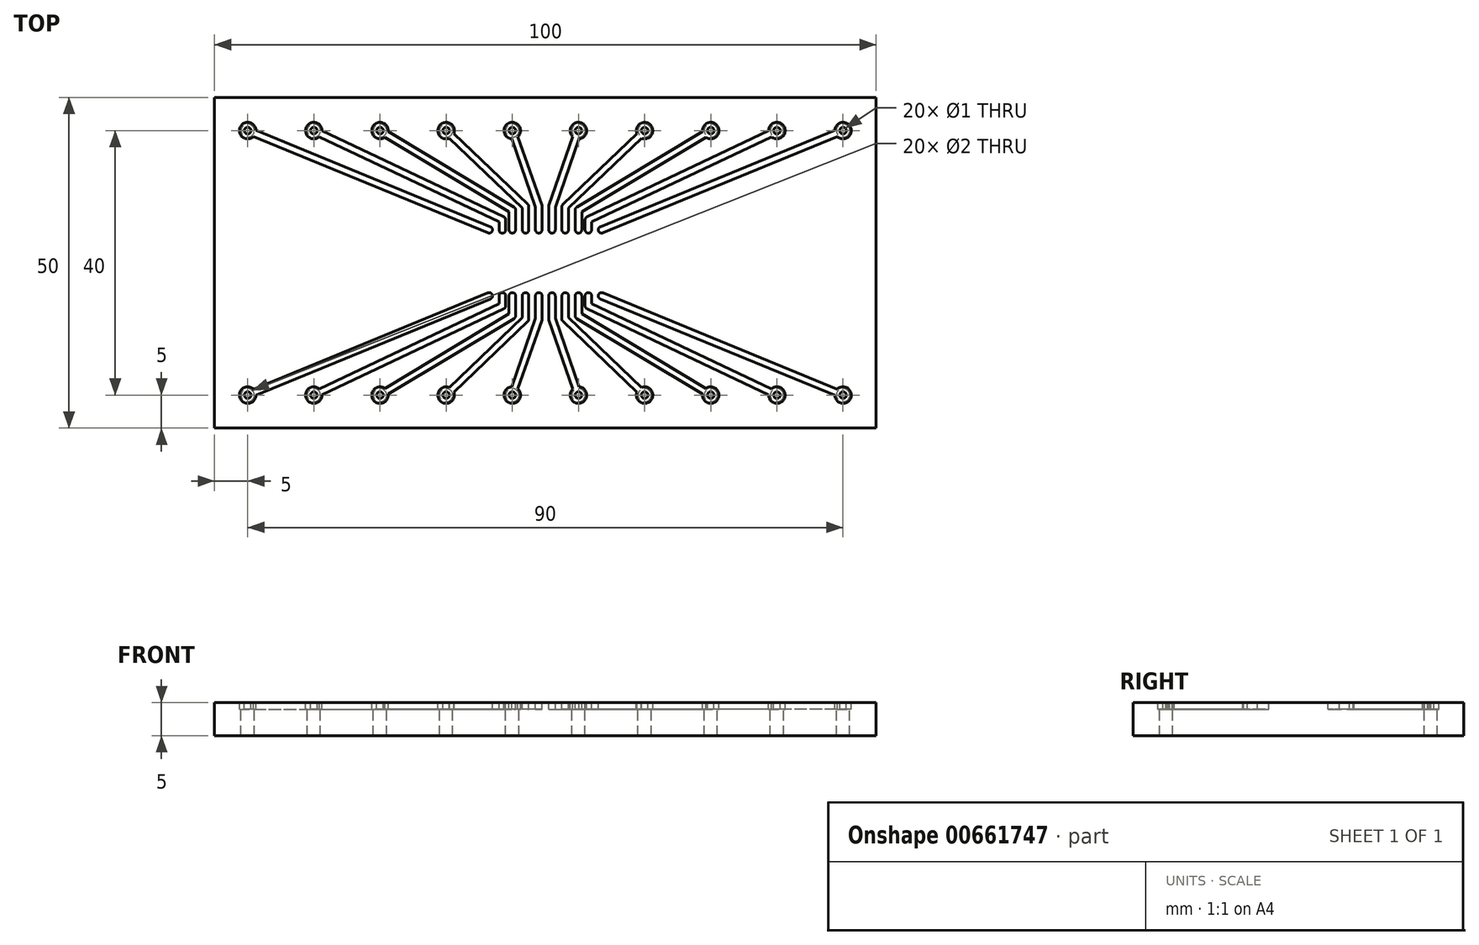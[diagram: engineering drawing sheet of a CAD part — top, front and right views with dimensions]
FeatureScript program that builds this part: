
annotation { "Feature Type Name" : "Feature", "Feature Type Description" : "" }
export const myFeature = defineFeature(function(context is Context, id is Id, definition is map)
    precondition{}
    {
        {
            var Q0;
            Q0=qCreatedBy(makeId("Top.planeOp"),FACE);
            var sketch = newSketch(context, id + "F0", { "sketchPlane" : qUnion([Q0])});
            skLineSegment(sketch, "E0.bottom", {"start": v(50, -25) * mm, "end": v(-50, -25) * mm});
            skLineSegment(sketch, "E0.top", {"start": v(50, 25) * mm, "end": v(-50, 25) * mm});
            skLineSegment(sketch, "E0.left", {"start": v(50, -25) * mm, "end": v(50, 25) * mm});
            skLineSegment(sketch, "E0.right", {"start": v(-50, -25) * mm, "end": v(-50, 25) * mm});
            skPoint(sketch, "E0.middle", {"position": v(0, 0) * mm});
            skSolve(sketch);
        }
        {
            var Q0;
            Q0=makeQuery(id+"F0.imprint","IMPRINT",FACE,{"disambiguationData":[TD([[makeQuery(id+"F0.imprint","IMPRINT",EDGE,{"derivedFrom":sQuery(id+"F0.wireOp",EDGE,"E0.bottom")}),-1.0]])]});
            extrude(context, id + "F1", {"entities" : qUnion([Q0]), "depth" : 5 * mm, "offsetDistance" : 25 * mm});
        }
        {
            var Q0;
            Q0=makeQuery(id+"F1.opExtrude","CAP_FACE",FACE,{"disambiguationData":[OSD([sQuery(id+"F0.wireOp",EDGE,"E0.bottom"),sQuery(id+"F0.wireOp",EDGE,"E0.top"),sQuery(id+"F0.wireOp",EDGE,"E0.left"),sQuery(id+"F0.wireOp",EDGE,"E0.right")])],"isStart":false});
            var sketch = newSketch(context, id + "F2", { "sketchPlane" : qUnion([Q0])});
            skPoint(sketch, "E1", {"position": v(-45, 20) * mm});
            skPoint(sketch, "E2.0.1.0", {"position": v(-45, -20) * mm});
            skPoint(sketch, "E2.1.0.0", {"position": v(-35, 20) * mm});
            skPoint(sketch, "E2.1.1.0", {"position": v(-35, -20) * mm});
            skPoint(sketch, "E2.2.0.0", {"position": v(-25, 20) * mm});
            skPoint(sketch, "E2.2.1.0", {"position": v(-25, -20) * mm});
            skPoint(sketch, "E2.3.0.0", {"position": v(-15, 20) * mm});
            skPoint(sketch, "E2.3.1.0", {"position": v(-15, -20) * mm});
            skPoint(sketch, "E2.4.0.0", {"position": v(-5, 20) * mm});
            skPoint(sketch, "E2.4.1.0", {"position": v(-5, -20) * mm});
            skPoint(sketch, "E2.5.0.0", {"position": v(5, 20) * mm});
            skPoint(sketch, "E2.5.1.0", {"position": v(5, -20) * mm});
            skPoint(sketch, "E2.6.0.0", {"position": v(15, 20) * mm});
            skPoint(sketch, "E2.6.1.0", {"position": v(15, -20) * mm});
            skPoint(sketch, "E2.7.0.0", {"position": v(25, 20) * mm});
            skPoint(sketch, "E2.7.1.0", {"position": v(25, -20) * mm});
            skPoint(sketch, "E2.8.0.0", {"position": v(35, 20) * mm});
            skPoint(sketch, "E2.8.1.0", {"position": v(35, -20) * mm});
            skPoint(sketch, "E2.9.0.0", {"position": v(45, 20) * mm});
            skPoint(sketch, "E2.9.1.0", {"position": v(45, -20) * mm});
            skLineSegment(sketch, "E2.direction1", {"start": v(-45, 20) * mm, "end": v(-35, 20) * mm, "construction": true});
            skLineSegment(sketch, "E2.direction2", {"start": v(-45, 20) * mm, "end": v(-45, -20) * mm, "construction": true});
            skLineSegment(sketch, "E3.bottom", {"start": v(10.5, 5) * mm, "end": v(-9.5, 5) * mm});
            skLineSegment(sketch, "E3.top", {"start": v(9.5, -5) * mm, "end": v(-10.5, -5) * mm});
            skPoint(sketch, "E3.middle", {"position": v(0, 0) * mm});
            skPoint(sketch, "E4", {"position": v(-8.5, 5) * mm});
            skPoint(sketch, "E5.0.1.0", {"position": v(-9, -5) * mm});
            skPoint(sketch, "E5.1.0.0", {"position": v(-6.5, 5) * mm});
            skPoint(sketch, "E5.1.1.0", {"position": v(-7, -5) * mm});
            skPoint(sketch, "E5.2.0.0", {"position": v(-5, 5) * mm});
            skPoint(sketch, "E5.2.1.0", {"position": v(-5, -5) * mm});
            skPoint(sketch, "E5.3.0.0", {"position": v(-3, 5) * mm});
            skPoint(sketch, "E5.3.1.0", {"position": v(-3, -5) * mm});
            skPoint(sketch, "E5.4.0.0", {"position": v(-1, 5) * mm});
            skPoint(sketch, "E5.4.1.0", {"position": v(-1, -5) * mm});
            skPoint(sketch, "E5.5.0.0", {"position": v(1, 5) * mm});
            skPoint(sketch, "E5.5.1.0", {"position": v(1, -5) * mm});
            skPoint(sketch, "E5.6.0.0", {"position": v(3, 5) * mm});
            skPoint(sketch, "E5.6.1.0", {"position": v(3, -5) * mm});
            skPoint(sketch, "E5.7.0.0", {"position": v(5, 5) * mm});
            skPoint(sketch, "E5.7.1.0", {"position": v(5, -5) * mm});
            skPoint(sketch, "E5.8.0.0", {"position": v(7, 5) * mm});
            skPoint(sketch, "E5.8.1.0", {"position": v(7, -5) * mm});
            skPoint(sketch, "E5.9.0.0", {"position": v(9, 5) * mm});
            skPoint(sketch, "E5.9.1.0", {"position": v(9, -5) * mm});
            skLineSegment(sketch, "E5.direction1", {"start": v(-8.5, 5) * mm, "end": v(-6.5, 5) * mm, "construction": true});
            skLineSegment(sketch, "E6", {"start": v(-45, 20) * mm, "end": v(-8.5, 5) * mm});
            skArc(sketch, "E7.0.startCap", {"start": v(-45.2, 19.54) * mm, "mid": v(-45.46, 20.2) * mm, "end": v(-44.8, 20.46) * mm});
            skArc(sketch, "E7.0.endCap", {"start": v(-8.3, 5.46) * mm, "mid": v(-8.04, 4.8) * mm, "end": v(-8.69, 4.54) * mm});
            skLineSegment(sketch, "E7.0.left", {"start": v(-44.8, 20.46) * mm, "end": v(-8.3, 5.46) * mm});
            skLineSegment(sketch, "E7.0.right", {"start": v(-45.2, 19.54) * mm, "end": v(-8.69, 4.54) * mm});
            skLineSegment(sketch, "E8", {"start": v(-6.5, 5) * mm, "end": v(-6.5, 6.5) * mm});
            skLineSegment(sketch, "E9", {"start": v(-35, 20) * mm, "end": v(-6.5, 6.5) * mm});
            skArc(sketch, "E10.0.startCap", {"start": v(-6, 5) * mm, "mid": v(-6.5, 4.5) * mm, "end": v(-7, 5) * mm});
            skArc(sketch, "E10.0.endCap", {"start": v(-7, 6.5) * mm, "mid": v(-6.5, 7) * mm, "end": v(-6, 6.5) * mm});
            skLineSegment(sketch, "E10.0.left", {"start": v(-7, 5) * mm, "end": v(-7, 6.5) * mm});
            skLineSegment(sketch, "E10.0.right", {"start": v(-6, 5) * mm, "end": v(-6, 6.5) * mm});
            skArc(sketch, "E10.1.startCap", {"start": v(-35.21, 19.55) * mm, "mid": v(-35.45, 20.21) * mm, "end": v(-34.79, 20.45) * mm});
            skArc(sketch, "E10.1.endCap", {"start": v(-6.29, 6.95) * mm, "mid": v(-6.05, 6.29) * mm, "end": v(-6.71, 6.05) * mm});
            skLineSegment(sketch, "E10.1.left", {"start": v(-34.79, 20.45) * mm, "end": v(-6.29, 6.95) * mm});
            skLineSegment(sketch, "E10.1.right", {"start": v(-35.21, 19.55) * mm, "end": v(-6.71, 6.05) * mm});
            skLineSegment(sketch, "E11", {"start": v(-5, 5) * mm, "end": v(-5, 8) * mm});
            skLineSegment(sketch, "E12", {"start": v(-5, 8) * mm, "end": v(-25, 20) * mm});
            skLineSegment(sketch, "E13", {"start": v(-3, 5) * mm, "end": v(-3, 8.5) * mm});
            skLineSegment(sketch, "E14", {"start": v(-3, 8.5) * mm, "end": v(-15, 20) * mm});
            skLineSegment(sketch, "E15", {"start": v(-1, 5) * mm, "end": v(-1, 8.5) * mm});
            skLineSegment(sketch, "E16", {"start": v(-1, 8.5) * mm, "end": v(-5, 20) * mm});
            skArc(sketch, "E17.0.startCap", {"start": v(-4.5, 5) * mm, "mid": v(-5, 4.5) * mm, "end": v(-5.5, 5) * mm});
            skArc(sketch, "E17.0.endCap", {"start": v(-5.5, 8) * mm, "mid": v(-5, 8.5) * mm, "end": v(-4.5, 8) * mm});
            skLineSegment(sketch, "E17.0.left", {"start": v(-5.5, 5) * mm, "end": v(-5.5, 8) * mm});
            skLineSegment(sketch, "E17.0.right", {"start": v(-4.5, 5) * mm, "end": v(-4.5, 8) * mm});
            skArc(sketch, "E17.1.startCap", {"start": v(-2.65, 8.86) * mm, "mid": v(-2.64, 8.15) * mm, "end": v(-3.35, 8.14) * mm});
            skArc(sketch, "E17.1.endCap", {"start": v(-15.35, 19.64) * mm, "mid": v(-15.36, 20.35) * mm, "end": v(-14.65, 20.36) * mm});
            skLineSegment(sketch, "E17.1.left", {"start": v(-3.35, 8.14) * mm, "end": v(-15.35, 19.64) * mm});
            skLineSegment(sketch, "E17.1.right", {"start": v(-2.65, 8.86) * mm, "end": v(-14.65, 20.36) * mm});
            skArc(sketch, "E17.2.startCap", {"start": v(-0.53, 8.66) * mm, "mid": v(-0.84, 8.03) * mm, "end": v(-1.47, 8.34) * mm});
            skArc(sketch, "E17.2.endCap", {"start": v(-5.47, 19.84) * mm, "mid": v(-5.16, 20.47) * mm, "end": v(-4.53, 20.16) * mm});
            skLineSegment(sketch, "E17.2.left", {"start": v(-1.47, 8.34) * mm, "end": v(-5.47, 19.84) * mm});
            skLineSegment(sketch, "E17.2.right", {"start": v(-0.53, 8.66) * mm, "end": v(-4.53, 20.16) * mm});
            skArc(sketch, "E17.3.startCap", {"start": v(-2.5, 5) * mm, "mid": v(-3, 4.5) * mm, "end": v(-3.5, 5) * mm});
            skArc(sketch, "E17.3.endCap", {"start": v(-3.5, 8.5) * mm, "mid": v(-3, 9) * mm, "end": v(-2.5, 8.5) * mm});
            skLineSegment(sketch, "E17.3.left", {"start": v(-3.5, 5) * mm, "end": v(-3.5, 8.5) * mm});
            skLineSegment(sketch, "E17.3.right", {"start": v(-2.5, 5) * mm, "end": v(-2.5, 8.5) * mm});
            skArc(sketch, "E17.4.startCap", {"start": v(-0.5, 5) * mm, "mid": v(-1, 4.5) * mm, "end": v(-1.5, 5) * mm});
            skArc(sketch, "E17.4.endCap", {"start": v(-1.5, 8.5) * mm, "mid": v(-1, 9) * mm, "end": v(-0.5, 8.5) * mm});
            skLineSegment(sketch, "E17.4.left", {"start": v(-1.5, 5) * mm, "end": v(-1.5, 8.5) * mm});
            skLineSegment(sketch, "E17.4.right", {"start": v(-0.5, 5) * mm, "end": v(-0.5, 8.5) * mm});
            skArc(sketch, "E17.5.startCap", {"start": v(-4.74, 8.43) * mm, "mid": v(-4.57, 7.74) * mm, "end": v(-5.26, 7.57) * mm});
            skArc(sketch, "E17.5.endCap", {"start": v(-25.26, 19.57) * mm, "mid": v(-25.43, 20.26) * mm, "end": v(-24.74, 20.43) * mm});
            skLineSegment(sketch, "E17.5.left", {"start": v(-5.26, 7.57) * mm, "end": v(-25.26, 19.57) * mm});
            skLineSegment(sketch, "E17.5.right", {"start": v(-4.74, 8.43) * mm, "end": v(-24.74, 20.43) * mm});
            skLineSegment(sketch, "E18.MirrorCS", {"start": v(44.8, 20.46) * mm, "end": v(8.3, 5.46) * mm});
            skLineSegment(sketch, "E19.MirrorCS", {"start": v(35, 20) * mm, "end": v(6.5, 6.5) * mm});
            skArc(sketch, "E20.MirrorCS", {"start": v(7, 6.5) * mm, "mid": v(6.5, 7) * mm, "end": v(6, 6.5) * mm});
            skLineSegment(sketch, "E21.MirrorCS", {"start": v(3.5, 5) * mm, "end": v(3.5, 8.5) * mm});
            skArc(sketch, "E22.MirrorCS", {"start": v(5.5, 8) * mm, "mid": v(5, 8.5) * mm, "end": v(4.5, 8) * mm});
            skLineSegment(sketch, "E23.MirrorCS", {"start": v(4.74, 8.43) * mm, "end": v(24.74, 20.43) * mm});
            skArc(sketch, "E24.MirrorCS", {"start": v(5.47, 19.84) * mm, "mid": v(5.16, 20.47) * mm, "end": v(4.53, 20.16) * mm});
            skArc(sketch, "E25.MirrorCS", {"start": v(0.5, 5) * mm, "mid": v(1, 4.5) * mm, "end": v(1.5, 5) * mm});
            skLineSegment(sketch, "E26.MirrorCS", {"start": v(7, 5) * mm, "end": v(7, 6.5) * mm});
            skLineSegment(sketch, "E27.MirrorCS", {"start": v(2.5, 5) * mm, "end": v(2.5, 8.5) * mm});
            skLineSegment(sketch, "E28.MirrorCS", {"start": v(5.5, 5) * mm, "end": v(5.5, 8) * mm});
            skLineSegment(sketch, "E29.MirrorCS", {"start": v(5, 5) * mm, "end": v(5, 8) * mm});
            skLineSegment(sketch, "E30.MirrorCS", {"start": v(4.5, 5) * mm, "end": v(4.5, 8) * mm});
            skLineSegment(sketch, "E31.MirrorCS", {"start": v(6, 5) * mm, "end": v(6, 6.5) * mm});
            skArc(sketch, "E32.MirrorCS", {"start": v(1.5, 8.5) * mm, "mid": v(1, 9) * mm, "end": v(0.5, 8.5) * mm});
            skLineSegment(sketch, "E33.MirrorCS", {"start": v(5, 8) * mm, "end": v(25, 20) * mm});
            skArc(sketch, "E34.MirrorCS", {"start": v(2.65, 8.86) * mm, "mid": v(2.64, 8.15) * mm, "end": v(3.35, 8.14) * mm});
            skArc(sketch, "E35.MirrorCS", {"start": v(35.21, 19.55) * mm, "mid": v(35.45, 20.21) * mm, "end": v(34.79, 20.45) * mm});
            skLineSegment(sketch, "E36.MirrorCS", {"start": v(1.47, 8.34) * mm, "end": v(5.47, 19.84) * mm});
            skLineSegment(sketch, "E37.MirrorCS", {"start": v(45, 20) * mm, "end": v(8.5, 5) * mm});
            skArc(sketch, "E38.MirrorCS", {"start": v(8.3, 5.46) * mm, "mid": v(8.04, 4.8) * mm, "end": v(8.69, 4.54) * mm});
            skLineSegment(sketch, "E39.MirrorCS", {"start": v(6.5, 5) * mm, "end": v(6.5, 6.5) * mm});
            skLineSegment(sketch, "E40.MirrorCS", {"start": v(3, 5) * mm, "end": v(3, 8.5) * mm});
            skLineSegment(sketch, "E41.MirrorCS", {"start": v(45.2, 19.54) * mm, "end": v(8.69, 4.54) * mm});
            skArc(sketch, "E42.MirrorCS", {"start": v(6, 5) * mm, "mid": v(6.5, 4.5) * mm, "end": v(7, 5) * mm});
            skArc(sketch, "E43.MirrorCS", {"start": v(15.35, 19.64) * mm, "mid": v(15.36, 20.35) * mm, "end": v(14.65, 20.36) * mm});
            skLineSegment(sketch, "E44.MirrorCS", {"start": v(1.5, 5) * mm, "end": v(1.5, 8.5) * mm});
            skArc(sketch, "E45.MirrorCS", {"start": v(6.29, 6.95) * mm, "mid": v(6.05, 6.29) * mm, "end": v(6.71, 6.05) * mm});
            skLineSegment(sketch, "E46.MirrorCS", {"start": v(0.53, 8.66) * mm, "end": v(4.53, 20.16) * mm});
            skLineSegment(sketch, "E47.MirrorCS", {"start": v(0.5, 5) * mm, "end": v(0.5, 8.5) * mm});
            skArc(sketch, "E48.MirrorCS", {"start": v(4.74, 8.43) * mm, "mid": v(4.57, 7.74) * mm, "end": v(5.26, 7.57) * mm});
            skLineSegment(sketch, "E49.MirrorCS", {"start": v(3, 8.5) * mm, "end": v(15, 20) * mm});
            skLineSegment(sketch, "E50.MirrorCS", {"start": v(3.35, 8.14) * mm, "end": v(15.35, 19.64) * mm});
            skLineSegment(sketch, "E51.MirrorCS", {"start": v(34.79, 20.45) * mm, "end": v(6.29, 6.95) * mm});
            skArc(sketch, "E52.MirrorCS", {"start": v(2.5, 5) * mm, "mid": v(3, 4.5) * mm, "end": v(3.5, 5) * mm});
            skArc(sketch, "E53.MirrorCS", {"start": v(25.26, 19.57) * mm, "mid": v(25.43, 20.26) * mm, "end": v(24.74, 20.43) * mm});
            skLineSegment(sketch, "E54.MirrorCS", {"start": v(1, 5) * mm, "end": v(1, 8.5) * mm});
            skLineSegment(sketch, "E55.MirrorCS", {"start": v(2.65, 8.86) * mm, "end": v(14.65, 20.36) * mm});
            skLineSegment(sketch, "E56.MirrorCS", {"start": v(35.21, 19.55) * mm, "end": v(6.71, 6.05) * mm});
            skArc(sketch, "E57.MirrorCS", {"start": v(3.5, 8.5) * mm, "mid": v(3, 9) * mm, "end": v(2.5, 8.5) * mm});
            skArc(sketch, "E58.MirrorCS", {"start": v(4.5, 5) * mm, "mid": v(5, 4.5) * mm, "end": v(5.5, 5) * mm});
            skLineSegment(sketch, "E59.MirrorCS", {"start": v(5.26, 7.57) * mm, "end": v(25.26, 19.57) * mm});
            skLineSegment(sketch, "E60.MirrorCS", {"start": v(1, 8.5) * mm, "end": v(5, 20) * mm});
            skArc(sketch, "E61.MirrorCS", {"start": v(0.53, 8.66) * mm, "mid": v(0.84, 8.03) * mm, "end": v(1.47, 8.34) * mm});
            skArc(sketch, "E62.MirrorCS", {"start": v(45.2, 19.54) * mm, "mid": v(45.46, 20.2) * mm, "end": v(44.8, 20.46) * mm});
            skArc(sketch, "E63.MirrorCS", {"start": v(2.5, -5) * mm, "mid": v(3, -4.5) * mm, "end": v(3.5, -5) * mm});
            skArc(sketch, "E64.MirrorCS", {"start": v(-3.5, -8.5) * mm, "mid": v(-3, -9) * mm, "end": v(-2.5, -8.5) * mm});
            skLineSegment(sketch, "E65.MirrorCS", {"start": v(44.8, -20.46) * mm, "end": v(8.3, -5.46) * mm});
            skLineSegment(sketch, "E66.MirrorCS", {"start": v(4.74, -8.43) * mm, "end": v(24.74, -20.43) * mm});
            skArc(sketch, "E67.MirrorCS", {"start": v(2.65, -8.86) * mm, "mid": v(2.64, -8.15) * mm, "end": v(3.35, -8.14) * mm});
            skLineSegment(sketch, "E68.MirrorCS", {"start": v(6.5, -5) * mm, "end": v(6.5, -6.5) * mm});
            skLineSegment(sketch, "E69.MirrorCS", {"start": v(3.35, -8.14) * mm, "end": v(15.35, -19.64) * mm});
            skPoint(sketch, "E70.MirrorP", {"position": v(-6.5, -5) * mm});
            skLineSegment(sketch, "E71.MirrorCS", {"start": v(-8.5, -5) * mm, "end": v(-6.5, -5) * mm, "construction": true});
            skLineSegment(sketch, "E72.MirrorCS", {"start": v(2.65, -8.86) * mm, "end": v(14.65, -20.36) * mm});
            skLineSegment(sketch, "E73.MirrorCS", {"start": v(-5.5, -5) * mm, "end": v(-5.5, -8) * mm});
            skLineSegment(sketch, "E74.MirrorCS", {"start": v(-7, -5) * mm, "end": v(-7, -6.5) * mm});
            skLineSegment(sketch, "E75.MirrorCS", {"start": v(-1.5, -5) * mm, "end": v(-1.5, -8.5) * mm});
            skArc(sketch, "E76.MirrorCS", {"start": v(-2.65, -8.86) * mm, "mid": v(-2.64, -8.15) * mm, "end": v(-3.35, -8.14) * mm});
            skLineSegment(sketch, "E77.MirrorCS", {"start": v(5.5, -5) * mm, "end": v(5.5, -8) * mm});
            skArc(sketch, "E78.MirrorCS", {"start": v(-4.74, -8.43) * mm, "mid": v(-4.57, -7.74) * mm, "end": v(-5.26, -7.57) * mm});
            skLineSegment(sketch, "E79.MirrorCS", {"start": v(1.5, -5) * mm, "end": v(1.5, -8.5) * mm});
            skLineSegment(sketch, "E80.MirrorCS", {"start": v(4.5, -5) * mm, "end": v(4.5, -8) * mm});
            skArc(sketch, "E81.MirrorCS", {"start": v(-6.29, -6.95) * mm, "mid": v(-6.05, -6.29) * mm, "end": v(-6.71, -6.05) * mm});
            skLineSegment(sketch, "E82.MirrorCS", {"start": v(1, -8.5) * mm, "end": v(5, -20) * mm});
            skLineSegment(sketch, "E83.MirrorCS", {"start": v(0.53, -8.66) * mm, "end": v(4.53, -20.16) * mm});
            skLineSegment(sketch, "E84.MirrorCS", {"start": v(-3, -5) * mm, "end": v(-3, -8.5) * mm});
            skLineSegment(sketch, "E85.MirrorCS", {"start": v(-2.65, -8.86) * mm, "end": v(-14.65, -20.36) * mm});
            skLineSegment(sketch, "E86.MirrorCS", {"start": v(-45, -20) * mm, "end": v(-8.5, -5) * mm});
            skArc(sketch, "E87.MirrorCS", {"start": v(45.2, -19.54) * mm, "mid": v(45.46, -20.2) * mm, "end": v(44.8, -20.46) * mm});
            skArc(sketch, "E88.MirrorCS", {"start": v(-2.5, -5) * mm, "mid": v(-3, -4.5) * mm, "end": v(-3.5, -5) * mm});
            skLineSegment(sketch, "E89.MirrorCS", {"start": v(-4.74, -8.43) * mm, "end": v(-24.74, -20.43) * mm});
            skArc(sketch, "E90.MirrorCS", {"start": v(5.5, -8) * mm, "mid": v(5, -8.5) * mm, "end": v(4.5, -8) * mm});
            skLineSegment(sketch, "E91.MirrorCS", {"start": v(5, -8) * mm, "end": v(25, -20) * mm});
            skArc(sketch, "E92.MirrorCS", {"start": v(-45.2, -19.54) * mm, "mid": v(-45.46, -20.2) * mm, "end": v(-44.8, -20.46) * mm});
            skArc(sketch, "E93.MirrorCS", {"start": v(8.3, -5.46) * mm, "mid": v(8.04, -4.8) * mm, "end": v(8.69, -4.54) * mm});
            skLineSegment(sketch, "E94.MirrorCS", {"start": v(3, -8.5) * mm, "end": v(15, -20) * mm});
            skLineSegment(sketch, "E95.MirrorCS", {"start": v(-1, -8.5) * mm, "end": v(-5, -20) * mm});
            skLineSegment(sketch, "E96.MirrorCS", {"start": v(1, -5) * mm, "end": v(1, -8.5) * mm});
            skLineSegment(sketch, "E97.MirrorCS", {"start": v(-2.5, -5) * mm, "end": v(-2.5, -8.5) * mm});
            skArc(sketch, "E98.MirrorCS", {"start": v(-8.3, -5.46) * mm, "mid": v(-8.04, -4.8) * mm, "end": v(-8.69, -4.54) * mm});
            skArc(sketch, "E99.MirrorCS", {"start": v(0.5, -5) * mm, "mid": v(1, -4.5) * mm, "end": v(1.5, -5) * mm});
            skLineSegment(sketch, "E100.MirrorCS", {"start": v(45.2, -19.54) * mm, "end": v(8.69, -4.54) * mm});
            skLineSegment(sketch, "E101.MirrorCS", {"start": v(-44.8, -20.46) * mm, "end": v(-8.3, -5.46) * mm});
            skArc(sketch, "E102.MirrorCS", {"start": v(-5.5, -8) * mm, "mid": v(-5, -8.5) * mm, "end": v(-4.5, -8) * mm});
            skArc(sketch, "E103.MirrorCS", {"start": v(-7, -6.5) * mm, "mid": v(-6.5, -7) * mm, "end": v(-6, -6.5) * mm});
            skArc(sketch, "E104.MirrorCS", {"start": v(3.5, -8.5) * mm, "mid": v(3, -9) * mm, "end": v(2.5, -8.5) * mm});
            skArc(sketch, "E105.MirrorCS", {"start": v(-1.5, -8.5) * mm, "mid": v(-1, -9) * mm, "end": v(-0.5, -8.5) * mm});
            skLineSegment(sketch, "E106.MirrorCS", {"start": v(-6.5, -5) * mm, "end": v(-6.5, -6.5) * mm});
            skLineSegment(sketch, "E107.MirrorCS", {"start": v(-4.5, -5) * mm, "end": v(-4.5, -8) * mm});
            skLineSegment(sketch, "E108.MirrorCS", {"start": v(-45.2, -19.54) * mm, "end": v(-8.69, -4.54) * mm});
            skLineSegment(sketch, "E109.MirrorCS", {"start": v(2.5, -5) * mm, "end": v(2.5, -8.5) * mm});
            skLineSegment(sketch, "E110.MirrorCS", {"start": v(-0.5, -5) * mm, "end": v(-0.5, -8.5) * mm});
            skArc(sketch, "E111.MirrorCS", {"start": v(15.35, -19.64) * mm, "mid": v(15.36, -20.35) * mm, "end": v(14.65, -20.36) * mm});
            skLineSegment(sketch, "E112.MirrorCS", {"start": v(5, -5) * mm, "end": v(5, -8) * mm});
            skLineSegment(sketch, "E113.MirrorCS", {"start": v(-35, -20) * mm, "end": v(-6.5, -6.5) * mm});
            skArc(sketch, "E114.MirrorCS", {"start": v(-35.21, -19.55) * mm, "mid": v(-35.45, -20.21) * mm, "end": v(-34.79, -20.45) * mm});
            skLineSegment(sketch, "E115.MirrorCS", {"start": v(5.26, -7.57) * mm, "end": v(25.26, -19.57) * mm});
            skArc(sketch, "E116.MirrorCS", {"start": v(6.29, -6.95) * mm, "mid": v(6.05, -6.29) * mm, "end": v(6.71, -6.05) * mm});
            skLineSegment(sketch, "E117.MirrorCS", {"start": v(-5, -8) * mm, "end": v(-25, -20) * mm});
            skLineSegment(sketch, "E118.MirrorCS", {"start": v(-3.35, -8.14) * mm, "end": v(-15.35, -19.64) * mm});
            skArc(sketch, "E119.MirrorCS", {"start": v(0.53, -8.66) * mm, "mid": v(0.84, -8.03) * mm, "end": v(1.47, -8.34) * mm});
            skLineSegment(sketch, "E120.MirrorCS", {"start": v(-0.53, -8.66) * mm, "end": v(-4.53, -20.16) * mm});
            skArc(sketch, "E121.MirrorCS", {"start": v(-6, -5) * mm, "mid": v(-6.5, -4.5) * mm, "end": v(-7, -5) * mm});
            skLineSegment(sketch, "E122.MirrorCS", {"start": v(-5.26, -7.57) * mm, "end": v(-25.26, -19.57) * mm});
            skLineSegment(sketch, "E123.MirrorCS", {"start": v(3.5, -5) * mm, "end": v(3.5, -8.5) * mm});
            skArc(sketch, "E124.MirrorCS", {"start": v(1.5, -8.5) * mm, "mid": v(1, -9) * mm, "end": v(0.5, -8.5) * mm});
            skLineSegment(sketch, "E125.MirrorCS", {"start": v(-35.21, -19.55) * mm, "end": v(-6.71, -6.05) * mm});
            skLineSegment(sketch, "E126.MirrorCS", {"start": v(45, -20) * mm, "end": v(8.5, -5) * mm});
            skArc(sketch, "E127.MirrorCS", {"start": v(4.74, -8.43) * mm, "mid": v(4.57, -7.74) * mm, "end": v(5.26, -7.57) * mm});
            skLineSegment(sketch, "E128.MirrorCS", {"start": v(-1, -5) * mm, "end": v(-1, -8.5) * mm});
            skArc(sketch, "E129.MirrorCS", {"start": v(-5.47, -19.84) * mm, "mid": v(-5.16, -20.47) * mm, "end": v(-4.53, -20.16) * mm});
            skArc(sketch, "E130.MirrorCS", {"start": v(25.26, -19.57) * mm, "mid": v(25.43, -20.26) * mm, "end": v(24.74, -20.43) * mm});
            skLineSegment(sketch, "E131.MirrorCS", {"start": v(-3.5, -5) * mm, "end": v(-3.5, -8.5) * mm});
            skLineSegment(sketch, "E132.MirrorCS", {"start": v(35, -20) * mm, "end": v(6.5, -6.5) * mm});
            skArc(sketch, "E133.MirrorCS", {"start": v(5.47, -19.84) * mm, "mid": v(5.16, -20.47) * mm, "end": v(4.53, -20.16) * mm});
            skArc(sketch, "E134.MirrorCS", {"start": v(35.21, -19.55) * mm, "mid": v(35.45, -20.21) * mm, "end": v(34.79, -20.45) * mm});
            skLineSegment(sketch, "E135.MirrorCS", {"start": v(-45, -20) * mm, "end": v(-35, -20) * mm, "construction": true});
            skLineSegment(sketch, "E136.MirrorCS", {"start": v(3, -5) * mm, "end": v(3, -8.5) * mm});
            skLineSegment(sketch, "E137.MirrorCS", {"start": v(34.79, -20.45) * mm, "end": v(6.29, -6.95) * mm});
            skArc(sketch, "E138.MirrorCS", {"start": v(-4.5, -5) * mm, "mid": v(-5, -4.5) * mm, "end": v(-5.5, -5) * mm});
            skLineSegment(sketch, "E139.MirrorCS", {"start": v(35.21, -19.55) * mm, "end": v(6.71, -6.05) * mm});
            skArc(sketch, "E140.MirrorCS", {"start": v(-0.5, -5) * mm, "mid": v(-1, -4.5) * mm, "end": v(-1.5, -5) * mm});
            skLineSegment(sketch, "E141.MirrorCS", {"start": v(7, -5) * mm, "end": v(7, -6.5) * mm});
            skArc(sketch, "E142.MirrorCS", {"start": v(6, -5) * mm, "mid": v(6.5, -4.5) * mm, "end": v(7, -5) * mm});
            skLineSegment(sketch, "E143.MirrorCS", {"start": v(10.5, -5) * mm, "end": v(-9.5, -5) * mm});
            skLineSegment(sketch, "E144.MirrorCS", {"start": v(-6, -5) * mm, "end": v(-6, -6.5) * mm});
            skArc(sketch, "E145.MirrorCS", {"start": v(4.5, -5) * mm, "mid": v(5, -4.5) * mm, "end": v(5.5, -5) * mm});
            skLineSegment(sketch, "E146.MirrorCS", {"start": v(-5, -5) * mm, "end": v(-5, -8) * mm});
            skArc(sketch, "E147.MirrorCS", {"start": v(-15.35, -19.64) * mm, "mid": v(-15.36, -20.35) * mm, "end": v(-14.65, -20.36) * mm});
            skLineSegment(sketch, "E148.MirrorCS", {"start": v(-1.47, -8.34) * mm, "end": v(-5.47, -19.84) * mm});
            skArc(sketch, "E149.MirrorCS", {"start": v(-25.26, -19.57) * mm, "mid": v(-25.43, -20.26) * mm, "end": v(-24.74, -20.43) * mm});
            skArc(sketch, "E150.MirrorCS", {"start": v(7, -6.5) * mm, "mid": v(6.5, -7) * mm, "end": v(6, -6.5) * mm});
            skLineSegment(sketch, "E151.MirrorCS", {"start": v(6, -5) * mm, "end": v(6, -6.5) * mm});
            skLineSegment(sketch, "E152.MirrorCS", {"start": v(-34.79, -20.45) * mm, "end": v(-6.29, -6.95) * mm});
            skLineSegment(sketch, "E153.MirrorCS", {"start": v(1.47, -8.34) * mm, "end": v(5.47, -19.84) * mm});
            skLineSegment(sketch, "E154.MirrorCS", {"start": v(0.5, -5) * mm, "end": v(0.5, -8.5) * mm});
            skLineSegment(sketch, "E155.MirrorCS", {"start": v(-3, -8.5) * mm, "end": v(-15, -20) * mm});
            skArc(sketch, "E156.MirrorCS", {"start": v(-0.53, -8.66) * mm, "mid": v(-0.84, -8.03) * mm, "end": v(-1.47, -8.34) * mm});
            skCircle(sketch, "E157", {"center": v(-45, 20) * mm, "radius": 1.25 * mm});
            skCircle(sketch, "E158.0.1.0", {"center": v(-45, -20) * mm, "radius": 1.25 * mm});
            skCircle(sketch, "E158.1.0.0", {"center": v(-35, 20) * mm, "radius": 1.25 * mm});
            skCircle(sketch, "E158.1.1.0", {"center": v(-35, -20) * mm, "radius": 1.25 * mm});
            skCircle(sketch, "E158.2.0.0", {"center": v(-25, 20) * mm, "radius": 1.25 * mm});
            skCircle(sketch, "E158.2.1.0", {"center": v(-25, -20) * mm, "radius": 1.25 * mm});
            skCircle(sketch, "E158.3.0.0", {"center": v(-15, 20) * mm, "radius": 1.25 * mm});
            skCircle(sketch, "E158.3.1.0", {"center": v(-15, -20) * mm, "radius": 1.25 * mm});
            skCircle(sketch, "E158.4.0.0", {"center": v(-5, 20) * mm, "radius": 1.25 * mm});
            skCircle(sketch, "E158.4.1.0", {"center": v(-5, -20) * mm, "radius": 1.25 * mm});
            skCircle(sketch, "E158.5.0.0", {"center": v(5, 20) * mm, "radius": 1.25 * mm});
            skCircle(sketch, "E158.5.1.0", {"center": v(5, -20) * mm, "radius": 1.25 * mm});
            skCircle(sketch, "E158.6.0.0", {"center": v(15, 20) * mm, "radius": 1.25 * mm});
            skCircle(sketch, "E158.6.1.0", {"center": v(15, -20) * mm, "radius": 1.25 * mm});
            skCircle(sketch, "E158.7.0.0", {"center": v(25, 20) * mm, "radius": 1.25 * mm});
            skCircle(sketch, "E158.7.1.0", {"center": v(25, -20) * mm, "radius": 1.25 * mm});
            skCircle(sketch, "E158.8.0.0", {"center": v(35, 20) * mm, "radius": 1.25 * mm});
            skCircle(sketch, "E158.8.1.0", {"center": v(35, -20) * mm, "radius": 1.25 * mm});
            skCircle(sketch, "E158.9.0.0", {"center": v(45, 20) * mm, "radius": 1.25 * mm});
            skCircle(sketch, "E158.9.1.0", {"center": v(45, -20) * mm, "radius": 1.25 * mm});
            skSolve(sketch);
        }
        {
            var Q0;
            Q0=sQuery(id+"F2.wireOp",VERTEX,"E2.7.0.0");
            var Q1;
            Q1=sQuery(id+"F2.wireOp",VERTEX,"E2.6.1.0");
            var Q2;
            Q2=sQuery(id+"F2.wireOp",VERTEX,"E2.1.1.0");
            var Q3;
            Q3=sQuery(id+"F2.wireOp",VERTEX,"E2.9.0.0");
            var Q4;
            Q4=sQuery(id+"F2.wireOp",VERTEX,"E2.2.0.0");
            var Q5;
            Q5=sQuery(id+"F2.wireOp",VERTEX,"E2.7.1.0");
            var Q6;
            Q6=sQuery(id+"F2.wireOp",VERTEX,"E2.3.0.0");
            var Q7;
            Q7=sQuery(id+"F2.wireOp",VERTEX,"E2.4.0.0");
            var Q8;
            Q8=sQuery(id+"F2.wireOp",VERTEX,"E2.2.1.0");
            var Q9;
            Q9=sQuery(id+"F2.wireOp",VERTEX,"E2.6.0.0");
            var Q10;
            Q10=sQuery(id+"F2.wireOp",VERTEX,"E2.8.0.0");
            var Q11;
            Q11=sQuery(id+"F2.wireOp",VERTEX,"E2.0.1.0");
            var Q12;
            Q12=sQuery(id+"F2.wireOp",VERTEX,"E6.start");
            var Q13;
            Q13=sQuery(id+"F2.wireOp",VERTEX,"E2.8.1.0");
            var Q14;
            Q14=sQuery(id+"F2.wireOp",VERTEX,"E2.3.1.0");
            var Q15;
            Q15=sQuery(id+"F2.wireOp",VERTEX,"E2.5.0.0");
            var Q16;
            Q16=sQuery(id+"F2.wireOp",VERTEX,"E9.start");
            var Q17;
            Q17=sQuery(id+"F2.wireOp",VERTEX,"E2.5.1.0");
            var Q18;
            Q18=sQuery(id+"F2.wireOp",VERTEX,"E2.9.1.0");
            var Q19;
            Q19=sQuery(id+"F2.wireOp",VERTEX,"E2.4.1.0");
            var Q20;
            Q20=makeQuery(id+"F1.opExtrude","SWEPT_BODY",BODY,{"disambiguationData":[OSD([sQuery(id+"F0.wireOp",EDGE,"E0.bottom"),sQuery(id+"F0.wireOp",EDGE,"E0.top"),sQuery(id+"F0.wireOp",EDGE,"E0.left"),sQuery(id+"F0.wireOp",EDGE,"E0.right")])]});
            hole(context, id + "F3", {"style" : HoleStyle.SIMPLE, "endStyle" : HoleEndStyle.THROUGH, "holeDiameter" : 2 * mm, "majorDiameter" : 5 * mm, "isTappedThrough" : true, "tappedDepth" : 12 * mm, "tapClearance" : 3, "locations" : qUnion([Q0, Q1, Q2, Q3, Q4, Q5, Q6, Q7, Q8, Q9, Q10, Q11, Q12, Q13, Q14, Q15, Q16, Q17, Q18, Q19]), "scope" : qUnion([Q20])});
        }
        {
            var Q0;
            Q0 = qSketchRegion(id + "F2", true);
            extrude(context, id + "F4", {"entities" : qUnion([Q0]), "operationType" : NewBodyOperationType.REMOVE, "oppositeDirection" : true, "depth" : 1 * mm, "offsetDistance" : 25 * mm});
        }
        {
            var Q0;
            Q0 = qSketchRegion(id + "F2", true);
            extrude(context, id + "F5", {"entities" : qUnion([Q0]), "oppositeDirection" : true, "depth" : 1 * mm, "offsetDistance" : 25 * mm});
        }
        {
            var Q0;
            Q0=sQuery(id+"F2.wireOp",VERTEX,"E2.1.0.0");
            var Q1;
            Q1=sQuery(id+"F2.wireOp",VERTEX,"E158.7.1.0.center");
            var Q2;
            Q2=sQuery(id+"F2.wireOp",VERTEX,"E158.8.0.0.center");
            var Q3;
            Q3=sQuery(id+"F2.wireOp",VERTEX,"E158.6.1.0.center");
            var Q4;
            Q4=sQuery(id+"F2.wireOp",VERTEX,"E158.3.0.0.center");
            var Q5;
            Q5=sQuery(id+"F2.wireOp",VERTEX,"E158.5.0.0.center");
            var Q6;
            Q6=sQuery(id+"F2.wireOp",VERTEX,"E2.9.1.0");
            var Q7;
            Q7=sQuery(id+"F2.wireOp",VERTEX,"E158.6.0.0.center");
            var Q8;
            Q8=sQuery(id+"F2.wireOp",VERTEX,"E158.8.1.0.center");
            var Q9;
            Q9=sQuery(id+"F2.wireOp",VERTEX,"E2.3.1.0");
            var Q10;
            Q10=sQuery(id+"F2.wireOp",VERTEX,"E158.4.0.0.center");
            var Q11;
            Q11=sQuery(id+"F2.wireOp",VERTEX,"E158.1.1.0.center");
            var Q12;
            Q12=sQuery(id+"F2.wireOp",VERTEX,"E2.2.1.0");
            var Q13;
            Q13=sQuery(id+"F2.wireOp",VERTEX,"E158.5.1.0.center");
            var Q14;
            Q14=sQuery(id+"F2.wireOp",VERTEX,"E1");
            var Q15;
            Q15=sQuery(id+"F2.wireOp",VERTEX,"E158.9.0.0.center");
            var Q16;
            Q16=sQuery(id+"F2.wireOp",VERTEX,"E2.0.1.0");
            var Q17;
            Q17=sQuery(id+"F2.wireOp",VERTEX,"E2.4.1.0");
            var Q18;
            Q18=sQuery(id+"F2.wireOp",VERTEX,"E2.2.0.0");
            var Q19;
            Q19=sQuery(id+"F2.wireOp",VERTEX,"E158.7.0.0.center");
            var Q20;
            Q20=makeQuery(id+"F5.opExtrude","SWEPT_BODY",BODY,{"disambiguationData":[OSD([sQuery(id+"F2.wireOp",EDGE,"E10.0.startCap"),sQuery(id+"F2.wireOp",EDGE,"E10.0.left"),sQuery(id+"F2.wireOp",EDGE,"E10.0.right"),sQuery(id+"F2.wireOp",EDGE,"E10.1.endCap"),sQuery(id+"F2.wireOp",EDGE,"E10.1.left"),sQuery(id+"F2.wireOp",EDGE,"E10.1.right"),sQuery(id+"F2.wireOp",EDGE,"E158.1.0.0")])]});
            var Q21;
            Q21=makeQuery(id+"F5.opExtrude","SWEPT_BODY",BODY,{"disambiguationData":[OSD([sQuery(id+"F2.wireOp",EDGE,"E66.MirrorCS"),sQuery(id+"F2.wireOp",EDGE,"E77.MirrorCS"),sQuery(id+"F2.wireOp",EDGE,"E80.MirrorCS"),sQuery(id+"F2.wireOp",EDGE,"E115.MirrorCS"),sQuery(id+"F2.wireOp",EDGE,"E127.MirrorCS"),sQuery(id+"F2.wireOp",EDGE,"E145.MirrorCS"),sQuery(id+"F2.wireOp",EDGE,"E158.7.1.0")])]});
            var Q22;
            Q22=makeQuery(id+"F5.opExtrude","SWEPT_BODY",BODY,{"disambiguationData":[OSD([sQuery(id+"F2.wireOp",EDGE,"E26.MirrorCS"),sQuery(id+"F2.wireOp",EDGE,"E31.MirrorCS"),sQuery(id+"F2.wireOp",EDGE,"E42.MirrorCS"),sQuery(id+"F2.wireOp",EDGE,"E45.MirrorCS"),sQuery(id+"F2.wireOp",EDGE,"E51.MirrorCS"),sQuery(id+"F2.wireOp",EDGE,"E56.MirrorCS"),sQuery(id+"F2.wireOp",EDGE,"E158.8.0.0")])]});
            var Q23;
            Q23=makeQuery(id+"F5.opExtrude","SWEPT_BODY",BODY,{"disambiguationData":[OSD([sQuery(id+"F2.wireOp",EDGE,"E63.MirrorCS"),sQuery(id+"F2.wireOp",EDGE,"E69.MirrorCS"),sQuery(id+"F2.wireOp",EDGE,"E72.MirrorCS"),sQuery(id+"F2.wireOp",EDGE,"E104.MirrorCS"),sQuery(id+"F2.wireOp",EDGE,"E109.MirrorCS"),sQuery(id+"F2.wireOp",EDGE,"E123.MirrorCS"),sQuery(id+"F2.wireOp",EDGE,"E158.6.1.0")])]});
            var Q24;
            Q24=makeQuery(id+"F5.opExtrude","SWEPT_BODY",BODY,{"disambiguationData":[OSD([sQuery(id+"F2.wireOp",EDGE,"E17.1.left"),sQuery(id+"F2.wireOp",EDGE,"E17.1.right"),sQuery(id+"F2.wireOp",EDGE,"E17.3.startCap"),sQuery(id+"F2.wireOp",EDGE,"E17.3.endCap"),sQuery(id+"F2.wireOp",EDGE,"E17.3.left"),sQuery(id+"F2.wireOp",EDGE,"E17.3.right"),sQuery(id+"F2.wireOp",EDGE,"E158.3.0.0")])]});
            var Q25;
            Q25=makeQuery(id+"F5.opExtrude","SWEPT_BODY",BODY,{"disambiguationData":[OSD([sQuery(id+"F2.wireOp",EDGE,"E25.MirrorCS"),sQuery(id+"F2.wireOp",EDGE,"E36.MirrorCS"),sQuery(id+"F2.wireOp",EDGE,"E44.MirrorCS"),sQuery(id+"F2.wireOp",EDGE,"E46.MirrorCS"),sQuery(id+"F2.wireOp",EDGE,"E47.MirrorCS"),sQuery(id+"F2.wireOp",EDGE,"E61.MirrorCS"),sQuery(id+"F2.wireOp",EDGE,"E158.5.0.0")])]});
            var Q26;
            Q26=makeQuery(id+"F5.opExtrude","SWEPT_BODY",BODY,{"disambiguationData":[OSD([sQuery(id+"F2.wireOp",EDGE,"E65.MirrorCS"),sQuery(id+"F2.wireOp",EDGE,"E93.MirrorCS"),sQuery(id+"F2.wireOp",EDGE,"E100.MirrorCS"),sQuery(id+"F2.wireOp",EDGE,"E158.9.1.0")])]});
            var Q27;
            Q27=makeQuery(id+"F5.opExtrude","SWEPT_BODY",BODY,{"disambiguationData":[OSD([sQuery(id+"F2.wireOp",EDGE,"E21.MirrorCS"),sQuery(id+"F2.wireOp",EDGE,"E27.MirrorCS"),sQuery(id+"F2.wireOp",EDGE,"E50.MirrorCS"),sQuery(id+"F2.wireOp",EDGE,"E52.MirrorCS"),sQuery(id+"F2.wireOp",EDGE,"E55.MirrorCS"),sQuery(id+"F2.wireOp",EDGE,"E57.MirrorCS"),sQuery(id+"F2.wireOp",EDGE,"E158.6.0.0")])]});
            var Q28;
            Q28=makeQuery(id+"F5.opExtrude","SWEPT_BODY",BODY,{"disambiguationData":[OSD([sQuery(id+"F2.wireOp",EDGE,"E137.MirrorCS"),sQuery(id+"F2.wireOp",EDGE,"E139.MirrorCS"),sQuery(id+"F2.wireOp",EDGE,"E141.MirrorCS"),sQuery(id+"F2.wireOp",EDGE,"E142.MirrorCS"),sQuery(id+"F2.wireOp",EDGE,"E150.MirrorCS"),sQuery(id+"F2.wireOp",EDGE,"E151.MirrorCS"),sQuery(id+"F2.wireOp",EDGE,"E158.8.1.0")])]});
            var Q29;
            Q29=makeQuery(id+"F5.opExtrude","SWEPT_BODY",BODY,{"disambiguationData":[OSD([sQuery(id+"F2.wireOp",EDGE,"E76.MirrorCS"),sQuery(id+"F2.wireOp",EDGE,"E85.MirrorCS"),sQuery(id+"F2.wireOp",EDGE,"E88.MirrorCS"),sQuery(id+"F2.wireOp",EDGE,"E97.MirrorCS"),sQuery(id+"F2.wireOp",EDGE,"E118.MirrorCS"),sQuery(id+"F2.wireOp",EDGE,"E131.MirrorCS"),sQuery(id+"F2.wireOp",EDGE,"E158.3.1.0")])]});
            var Q30;
            Q30=makeQuery(id+"F5.opExtrude","SWEPT_BODY",BODY,{"disambiguationData":[OSD([sQuery(id+"F2.wireOp",EDGE,"E17.2.left"),sQuery(id+"F2.wireOp",EDGE,"E17.2.right"),sQuery(id+"F2.wireOp",EDGE,"E17.4.startCap"),sQuery(id+"F2.wireOp",EDGE,"E17.4.endCap"),sQuery(id+"F2.wireOp",EDGE,"E17.4.left"),sQuery(id+"F2.wireOp",EDGE,"E17.4.right"),sQuery(id+"F2.wireOp",EDGE,"E158.4.0.0")])]});
            var Q31;
            Q31=makeQuery(id+"F5.opExtrude","SWEPT_BODY",BODY,{"disambiguationData":[OSD([sQuery(id+"F2.wireOp",EDGE,"E74.MirrorCS"),sQuery(id+"F2.wireOp",EDGE,"E103.MirrorCS"),sQuery(id+"F2.wireOp",EDGE,"E121.MirrorCS"),sQuery(id+"F2.wireOp",EDGE,"E125.MirrorCS"),sQuery(id+"F2.wireOp",EDGE,"E144.MirrorCS"),sQuery(id+"F2.wireOp",EDGE,"E152.MirrorCS"),sQuery(id+"F2.wireOp",EDGE,"E158.1.1.0")])]});
            var Q32;
            Q32=makeQuery(id+"F5.opExtrude","SWEPT_BODY",BODY,{"disambiguationData":[OSD([sQuery(id+"F2.wireOp",EDGE,"E73.MirrorCS"),sQuery(id+"F2.wireOp",EDGE,"E89.MirrorCS"),sQuery(id+"F2.wireOp",EDGE,"E102.MirrorCS"),sQuery(id+"F2.wireOp",EDGE,"E107.MirrorCS"),sQuery(id+"F2.wireOp",EDGE,"E122.MirrorCS"),sQuery(id+"F2.wireOp",EDGE,"E138.MirrorCS"),sQuery(id+"F2.wireOp",EDGE,"E158.2.1.0")])]});
            var Q33;
            Q33=makeQuery(id+"F5.opExtrude","SWEPT_BODY",BODY,{"disambiguationData":[OSD([sQuery(id+"F2.wireOp",EDGE,"E79.MirrorCS"),sQuery(id+"F2.wireOp",EDGE,"E83.MirrorCS"),sQuery(id+"F2.wireOp",EDGE,"E99.MirrorCS"),sQuery(id+"F2.wireOp",EDGE,"E124.MirrorCS"),sQuery(id+"F2.wireOp",EDGE,"E153.MirrorCS"),sQuery(id+"F2.wireOp",EDGE,"E154.MirrorCS"),sQuery(id+"F2.wireOp",EDGE,"E158.5.1.0")])]});
            var Q34;
            Q34=makeQuery(id+"F5.opExtrude","SWEPT_BODY",BODY,{"disambiguationData":[OSD([sQuery(id+"F2.wireOp",EDGE,"E7.0.endCap"),sQuery(id+"F2.wireOp",EDGE,"E7.0.left"),sQuery(id+"F2.wireOp",EDGE,"E7.0.right"),sQuery(id+"F2.wireOp",EDGE,"E157")])]});
            var Q35;
            Q35=makeQuery(id+"F5.opExtrude","SWEPT_BODY",BODY,{"disambiguationData":[OSD([sQuery(id+"F2.wireOp",EDGE,"E18.MirrorCS"),sQuery(id+"F2.wireOp",EDGE,"E38.MirrorCS"),sQuery(id+"F2.wireOp",EDGE,"E41.MirrorCS"),sQuery(id+"F2.wireOp",EDGE,"E158.9.0.0")])]});
            var Q36;
            Q36=makeQuery(id+"F5.opExtrude","SWEPT_BODY",BODY,{"disambiguationData":[OSD([sQuery(id+"F2.wireOp",EDGE,"E98.MirrorCS"),sQuery(id+"F2.wireOp",EDGE,"E101.MirrorCS"),sQuery(id+"F2.wireOp",EDGE,"E108.MirrorCS"),sQuery(id+"F2.wireOp",EDGE,"E158.0.1.0")])]});
            var Q37;
            Q37=makeQuery(id+"F5.opExtrude","SWEPT_BODY",BODY,{"disambiguationData":[OSD([sQuery(id+"F2.wireOp",EDGE,"E75.MirrorCS"),sQuery(id+"F2.wireOp",EDGE,"E110.MirrorCS"),sQuery(id+"F2.wireOp",EDGE,"E120.MirrorCS"),sQuery(id+"F2.wireOp",EDGE,"E140.MirrorCS"),sQuery(id+"F2.wireOp",EDGE,"E148.MirrorCS"),sQuery(id+"F2.wireOp",EDGE,"E156.MirrorCS"),sQuery(id+"F2.wireOp",EDGE,"E158.4.1.0")])]});
            var Q38;
            Q38=makeQuery(id+"F5.opExtrude","SWEPT_BODY",BODY,{"disambiguationData":[OSD([sQuery(id+"F2.wireOp",EDGE,"E17.0.startCap"),sQuery(id+"F2.wireOp",EDGE,"E17.0.left"),sQuery(id+"F2.wireOp",EDGE,"E17.0.right"),sQuery(id+"F2.wireOp",EDGE,"E17.5.startCap"),sQuery(id+"F2.wireOp",EDGE,"E17.5.left"),sQuery(id+"F2.wireOp",EDGE,"E17.5.right"),sQuery(id+"F2.wireOp",EDGE,"E158.2.0.0")])]});
            var Q39;
            Q39=makeQuery(id+"F5.opExtrude","SWEPT_BODY",BODY,{"disambiguationData":[OSD([sQuery(id+"F2.wireOp",EDGE,"E23.MirrorCS"),sQuery(id+"F2.wireOp",EDGE,"E28.MirrorCS"),sQuery(id+"F2.wireOp",EDGE,"E30.MirrorCS"),sQuery(id+"F2.wireOp",EDGE,"E48.MirrorCS"),sQuery(id+"F2.wireOp",EDGE,"E58.MirrorCS"),sQuery(id+"F2.wireOp",EDGE,"E59.MirrorCS"),sQuery(id+"F2.wireOp",EDGE,"E158.7.0.0")])]});
            hole(context, id + "F6", {"style" : HoleStyle.SIMPLE, "endStyle" : HoleEndStyle.THROUGH, "holeDiameter" : 1 * mm, "majorDiameter" : 5 * mm, "isTappedThrough" : true, "tappedDepth" : 12 * mm, "tapClearance" : 3, "locations" : qUnion([Q0, Q1, Q2, Q3, Q4, Q5, Q6, Q7, Q8, Q9, Q10, Q11, Q12, Q13, Q14, Q15, Q16, Q17, Q18, Q19]), "scope" : qUnion([Q20, Q21, Q22, Q23, Q24, Q25, Q26, Q27, Q28, Q29, Q30, Q31, Q32, Q33, Q34, Q35, Q36, Q37, Q38, Q39])});
        }
    });
